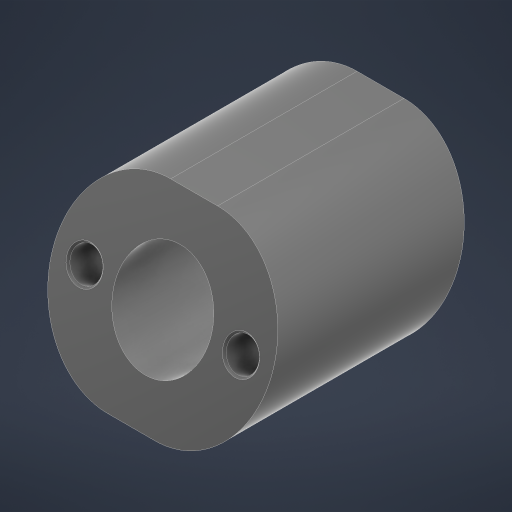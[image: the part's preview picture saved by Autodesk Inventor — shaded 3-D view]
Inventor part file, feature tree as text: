
AUTODESK INVENTOR PART (.ipt)
format: ipt  version: 2025 (Build 290162010, 162A)  size: 284,672 bytes
history: native  units: mm
features: extrude x6, sketch x6, fillet x2, chamfer x1
ambient origin geometry x8: Origin, YZ Plane, XZ Plane, XY Plane, X Axis, Y Axis, Z Axis, Center Point
bodies: Solid1 (feature_tree)
feature tree (15):
  extrude  "Extrusion1"  Depth=3.490659mm
  extrude  "Extrusion2"  Depth=22.4mm
  extrude  "Extrusion3"  Depth=2.0mm
  fillet  "Fillet1"  Radius=6.0mm
  fillet  "Fillet2"  Radius=6.0mm
  extrude  "Extrusion4"  Depth=11.5mm
  extrude  "Extrusion5"  Depth=11.0mm
  extrude  "Extrusion6"  Depth=2.0mm
  chamfer  "Chamfer1"  Distance=28.0mm
  sketch  "Sketch1"  dims[d1=37.5mm d2=3.490659mm]
  sketch  "Sketch2"  dims[d3=2.0mm d4=22.4mm]
  sketch  "Sketch3"  dims[d5=37.5mm d6=2.0mm d7=6.0mm d8=6.0mm]
  sketch  "Sketch4"  dims[d9=11.5mm d10=11.5mm]
  sketch  "Sketch5"  dims[d13=11.0mm d14=11.0mm]
  sketch  "Sketch6"  dims[d15=4.875mm d16=4.875mm d17=28.0mm d18=0.0mm d19=7.875mm d20=0.0mm d21=7.875mm d22=0.0mm d23=6.125mm d24=11.0mm d25=20.0mm d26=4.0mm d27=4.0mm d28=8.0mm d29=0.0mm d30=20.0mm d31=4.0mm d32=4.0mm d33=8.0mm d34=0.0mm d35=4.0mm d36=4.25mm d37=0.0mm d38=0.25mm d39=2.0mm d40=45.0deg]
